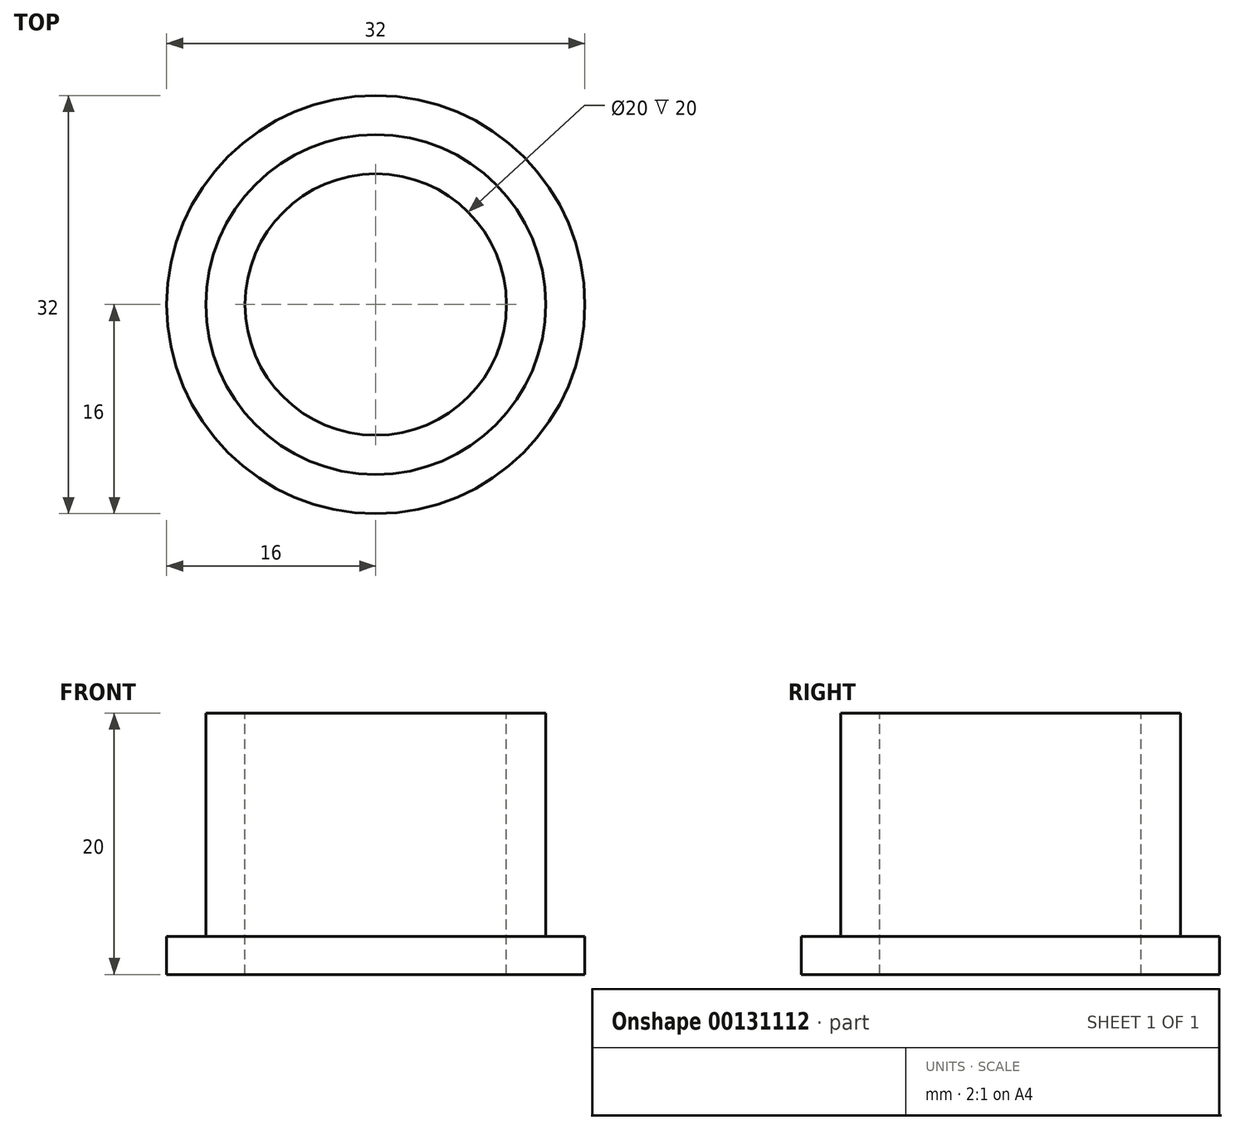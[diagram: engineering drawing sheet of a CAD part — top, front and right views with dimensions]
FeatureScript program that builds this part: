
annotation { "Feature Type Name" : "Feature", "Feature Type Description" : "" }
export const myFeature = defineFeature(function(context is Context, id is Id, definition is map)
    precondition{}
    {
        {
            var Q0;
            Q0=qCreatedBy(makeId("Front.planeOp"),FACE);
            var sketch = newSketch(context, id + "F0", { "sketchPlane" : qUnion([Q0])});
            skLineSegment(sketch, "E0", {"start": v(10, 0) * mm, "end": v(16, 0) * mm});
            skLineSegment(sketch, "E1", {"start": v(16, 0) * mm, "end": v(16, 2.9) * mm});
            skLineSegment(sketch, "E2", {"start": v(16, 2.9) * mm, "end": v(13, 2.9) * mm});
            skLineSegment(sketch, "E3", {"start": v(13, 2.9) * mm, "end": v(13, 20) * mm});
            skLineSegment(sketch, "E4", {"start": v(13, 20) * mm, "end": v(10, 20) * mm});
            skLineSegment(sketch, "E5", {"start": v(10, 20) * mm, "end": v(10, 0) * mm});
            skLineSegment(sketch, "E6", {"start": v(0, 4.55) * mm, "end": v(0, 0) * mm});
            skSolve(sketch);
        }
        {
            var Q0;
            Q0=makeQuery(id+"F0.imprint","IMPRINT",FACE,{"disambiguationData":[TD([[makeQuery(id+"F0.imprint","IMPRINT",EDGE,{"derivedFrom":sQuery(id+"F0.wireOp",EDGE,"E0")}),1.0]])]});
            var Q1;
            Q1=sQuery(id+"F0.wireOp",EDGE,"E6");
            revolve(context, id + "F1", {"entities" : qUnion([Q0]), "axis" : qUnion([Q1]), "revolveType" : RevolveType.FULL});
        }
    });
